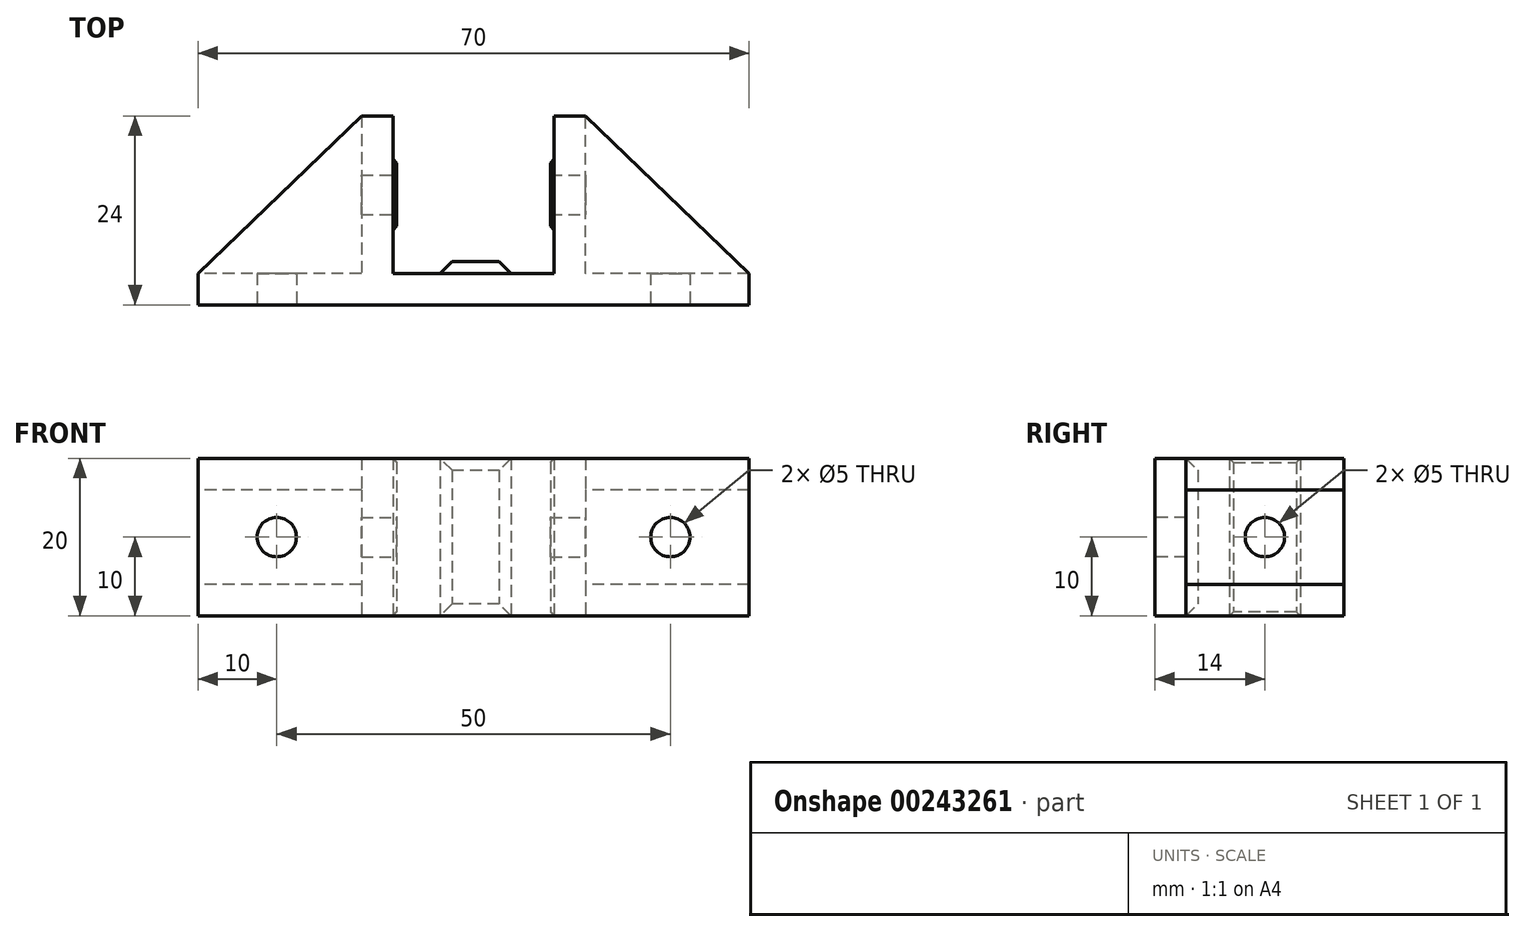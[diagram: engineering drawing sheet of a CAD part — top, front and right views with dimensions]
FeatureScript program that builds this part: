
annotation { "Feature Type Name" : "Feature", "Feature Type Description" : "" }
export const myFeature = defineFeature(function(context is Context, id is Id, definition is map)
    precondition{}
    {
        {
            var Q0;
            Q0=qCreatedBy(makeId("Top.planeOp"),FACE);
            var sketch = newSketch(context, id + "F0", { "sketchPlane" : qUnion([Q0])});
            skLineSegment(sketch, "E0", {"start": v(0, 0) * mm, "end": v(70, 0) * mm});
            skLineSegment(sketch, "E1", {"start": v(70, 0) * mm, "end": v(70, 4) * mm});
            skLineSegment(sketch, "E2", {"start": v(70, 4) * mm, "end": v(49.25, 4) * mm});
            skLineSegment(sketch, "E3", {"start": v(49.25, 4) * mm, "end": v(49.25, 24) * mm});
            skLineSegment(sketch, "E4", {"start": v(49.25, 24) * mm, "end": v(45.25, 24) * mm});
            skLineSegment(sketch, "E5", {"start": v(45.25, 24) * mm, "end": v(45.25, 18.5) * mm});
            skLineSegment(sketch, "E6", {"start": v(45.25, 4) * mm, "end": v(39.75, 4) * mm});
            skLineSegment(sketch, "E7", {"start": v(24.75, 4) * mm, "end": v(24.75, 9.5) * mm});
            skLineSegment(sketch, "E8", {"start": v(24.75, 24) * mm, "end": v(20.75, 24) * mm});
            skLineSegment(sketch, "E9", {"start": v(20.75, 24) * mm, "end": v(20.75, 4) * mm});
            skLineSegment(sketch, "E10", {"start": v(20.75, 4) * mm, "end": v(0, 4) * mm});
            skLineSegment(sketch, "E11", {"start": v(0, 4) * mm, "end": v(0, 0) * mm});
            skLineSegment(sketch, "E12", {"start": v(24.75, 18.5) * mm, "end": v(25.25, 18) * mm});
            skLineSegment(sketch, "E13", {"start": v(25.25, 18) * mm, "end": v(25.25, 10) * mm});
            skLineSegment(sketch, "E14", {"start": v(25.25, 10) * mm, "end": v(24.75, 9.5) * mm});
            skLineSegment(sketch, "E15", {"start": v(35, 4) * mm, "end": v(35, 25.01) * mm, "construction": true});
            skLineSegment(sketch, "E16.MirrorCS", {"start": v(44.75, 10) * mm, "end": v(45.25, 9.5) * mm});
            skLineSegment(sketch, "E17.MirrorCS", {"start": v(45.25, 18.5) * mm, "end": v(44.75, 18) * mm});
            skLineSegment(sketch, "E18.MirrorCS", {"start": v(44.75, 18) * mm, "end": v(44.75, 10) * mm});
            skLineSegment(sketch, "E19.trimOffspring", {"start": v(24.75, 18.5) * mm, "end": v(24.75, 24) * mm});
            skLineSegment(sketch, "E20.trimOffspring", {"start": v(45.25, 9.5) * mm, "end": v(45.25, 4) * mm});
            skLineSegment(sketch, "E21", {"start": v(30.75, 4) * mm, "end": v(32.25, 5.5) * mm});
            skLineSegment(sketch, "E22", {"start": v(32.25, 5.5) * mm, "end": v(38.25, 5.5) * mm});
            skLineSegment(sketch, "E23", {"start": v(38.25, 5.5) * mm, "end": v(39.75, 4) * mm});
            skLineSegment(sketch, "E24.trimOffspring", {"start": v(30.75, 4) * mm, "end": v(24.75, 4) * mm});
            skSolve(sketch);
        }
        {
            var Q0;
            Q0 = qSketchRegion(id + "F0", true);
            extrude(context, id + "F1", {"entities" : qUnion([Q0]), "depth" : 20 * mm});
        }
        {
            var Q0;
            Q0=makeQuery(id+"F1.opExtrude","SWEPT_FACE",FACE,{"disambiguationData":[OSD([sQuery(id+"F0.wireOp",EDGE,"E0")])]});
            var sketch = newSketch(context, id + "F2", { "sketchPlane" : qUnion([Q0])});
            skCircle(sketch, "E25", {"center": v(10, 10) * mm, "radius": 2.5 * mm});
            skPoint(sketch, "E25.centerSnap0", {"position": v(0, 10) * mm});
            skCircle(sketch, "E26", {"center": v(60, 10) * mm, "radius": 2.5 * mm});
            skSolve(sketch);
        }
        {
            var Q0;
            Q0 = qSketchRegion(id + "F2", true);
            extrude(context, id + "F3", {"entities" : qUnion([Q0]), "operationType" : NewBodyOperationType.REMOVE, "endBound" : BoundingType.THROUGH_ALL, "oppositeDirection" : true, "depth" : 25 * mm});
        }
        {
            var Q0;
            Q0=makeQuery(id+"F1.opExtrude","CAP_EDGE",EDGE,{"disambiguationData":[OSD([sQuery(id+"F0.wireOp",EDGE,"E13")])],"isStart":false});
            var Q1;
            Q1=makeQuery(id+"F1.opExtrude","CAP_EDGE",EDGE,{"disambiguationData":[OSD([sQuery(id+"F0.wireOp",EDGE,"E13")])],"isStart":true});
            var Q2;
            Q2=makeQuery(id+"F1.opExtrude","CAP_EDGE",EDGE,{"disambiguationData":[OSD([sQuery(id+"F0.wireOp",EDGE,"E18.MirrorCS")])],"isStart":false});
            var Q3;
            Q3=makeQuery(id+"F1.opExtrude","CAP_EDGE",EDGE,{"disambiguationData":[OSD([sQuery(id+"F0.wireOp",EDGE,"E18.MirrorCS")])],"isStart":true});
            chamfer(context, id + "F4", {"entities" : qUnion([Q0, Q1, Q2, Q3]), "width" : 0.5 * mm, "tangentPropagation" : true});
        }
        {
            var Q0;
            Q0=makeQuery(id+"F1.opExtrude","SWEPT_FACE",FACE,{"disambiguationData":[OSD([sQuery(id+"F0.wireOp",EDGE,"E3")])]});
            var sketch = newSketch(context, id + "F5", { "sketchPlane" : qUnion([Q0])});
            skLineSegment(sketch, "E27.0.0", {"start": v(18, 19.5) * mm, "end": v(18, 0.5) * mm, "construction": true});
            skLineSegment(sketch, "E27.0.1", {"start": v(18, 0.5) * mm, "end": v(10, 0.5) * mm, "construction": true});
            skLineSegment(sketch, "E27.0.2", {"start": v(10, 0.5) * mm, "end": v(10, 19.5) * mm, "construction": true});
            skLineSegment(sketch, "E27.0.3", {"start": v(10, 19.5) * mm, "end": v(18, 19.5) * mm, "construction": true});
            skCircle(sketch, "E28", {"center": v(14, 10) * mm, "radius": 2.5 * mm});
            skPoint(sketch, "E28.centerSnap0", {"position": v(10, 10) * mm});
            skPoint(sketch, "E28.centerSnap1", {"position": v(14, 19.5) * mm});
            skSolve(sketch);
        }
        {
            var Q0;
            Q0 = qSketchRegion(id + "F5", true);
            var Q1;
            Q1=makeQuery(id+"F1.opExtrude","SWEPT_FACE",FACE,{"disambiguationData":[OSD([sQuery(id+"F0.wireOp",EDGE,"E9")])]});
            extrude(context, id + "F6", {"entities" : qUnion([Q0]), "operationType" : NewBodyOperationType.REMOVE, "endBound" : BoundingType.UP_TO_SURFACE, "oppositeDirection" : true, "endBoundEntityFace" : qUnion([Q1]), "depth" : 25 * mm});
        }
        {
            var Q0;
            Q0=makeQuery(id+"F1.opExtrude","CAP_FACE",FACE,{"disambiguationData":[OSD([sQuery(id+"F0.wireOp",EDGE,"E0"),sQuery(id+"F0.wireOp",EDGE,"E1"),sQuery(id+"F0.wireOp",EDGE,"E2"),sQuery(id+"F0.wireOp",EDGE,"E3"),sQuery(id+"F0.wireOp",EDGE,"E4"),sQuery(id+"F0.wireOp",EDGE,"E5"),sQuery(id+"F0.wireOp",EDGE,"E6"),sQuery(id+"F0.wireOp",EDGE,"E7"),sQuery(id+"F0.wireOp",EDGE,"E8"),sQuery(id+"F0.wireOp",EDGE,"E9"),sQuery(id+"F0.wireOp",EDGE,"E10"),sQuery(id+"F0.wireOp",EDGE,"E11"),sQuery(id+"F0.wireOp",EDGE,"E12"),sQuery(id+"F0.wireOp",EDGE,"E13"),sQuery(id+"F0.wireOp",EDGE,"E14"),sQuery(id+"F0.wireOp",EDGE,"E16.MirrorCS"),sQuery(id+"F0.wireOp",EDGE,"E17.MirrorCS"),sQuery(id+"F0.wireOp",EDGE,"E18.MirrorCS"),sQuery(id+"F0.wireOp",EDGE,"E19.trimOffspring"),sQuery(id+"F0.wireOp",EDGE,"E20.trimOffspring"),sQuery(id+"F0.wireOp",EDGE,"E21"),sQuery(id+"F0.wireOp",EDGE,"E22"),sQuery(id+"F0.wireOp",EDGE,"E23"),sQuery(id+"F0.wireOp",EDGE,"E24.trimOffspring")])],"isStart":false});
            var sketch = newSketch(context, id + "F7", { "sketchPlane" : qUnion([Q0])});
            skLineSegment(sketch, "E29", {"start": v(20.75, 24) * mm, "end": v(0, 4) * mm});
            skLineSegment(sketch, "E30", {"start": v(0, 4) * mm, "end": v(20.75, 4) * mm});
            skLineSegment(sketch, "E31", {"start": v(20.75, 4) * mm, "end": v(20.75, 24) * mm});
            skLineSegment(sketch, "E32", {"start": v(49.25, 24) * mm, "end": v(49.25, 4) * mm});
            skLineSegment(sketch, "E33", {"start": v(49.25, 4) * mm, "end": v(70, 4) * mm});
            skLineSegment(sketch, "E34", {"start": v(70, 4) * mm, "end": v(49.25, 24) * mm});
            skSolve(sketch);
        }
        {
            var Q0;
            Q0 = qSketchRegion(id + "F7", true);
            extrude(context, id + "F8", {"entities" : qUnion([Q0]), "operationType" : NewBodyOperationType.ADD, "oppositeDirection" : true, "depth" : 4 * mm});
        }
        {
            var Q0;
            Q0=makeQuery(id+"F1.opExtrude","CAP_FACE",FACE,{"disambiguationData":[OSD([sQuery(id+"F0.wireOp",EDGE,"E0"),sQuery(id+"F0.wireOp",EDGE,"E1"),sQuery(id+"F0.wireOp",EDGE,"E2"),sQuery(id+"F0.wireOp",EDGE,"E3"),sQuery(id+"F0.wireOp",EDGE,"E4"),sQuery(id+"F0.wireOp",EDGE,"E5"),sQuery(id+"F0.wireOp",EDGE,"E6"),sQuery(id+"F0.wireOp",EDGE,"E7"),sQuery(id+"F0.wireOp",EDGE,"E8"),sQuery(id+"F0.wireOp",EDGE,"E9"),sQuery(id+"F0.wireOp",EDGE,"E10"),sQuery(id+"F0.wireOp",EDGE,"E11"),sQuery(id+"F0.wireOp",EDGE,"E12"),sQuery(id+"F0.wireOp",EDGE,"E13"),sQuery(id+"F0.wireOp",EDGE,"E14"),sQuery(id+"F0.wireOp",EDGE,"E16.MirrorCS"),sQuery(id+"F0.wireOp",EDGE,"E17.MirrorCS"),sQuery(id+"F0.wireOp",EDGE,"E18.MirrorCS"),sQuery(id+"F0.wireOp",EDGE,"E19.trimOffspring"),sQuery(id+"F0.wireOp",EDGE,"E20.trimOffspring"),sQuery(id+"F0.wireOp",EDGE,"E21"),sQuery(id+"F0.wireOp",EDGE,"E22"),sQuery(id+"F0.wireOp",EDGE,"E23"),sQuery(id+"F0.wireOp",EDGE,"E24.trimOffspring")])],"isStart":true});
            var sketch = newSketch(context, id + "F9", { "sketchPlane" : qUnion([Q0])});
            skLineSegment(sketch, "E35.0.0", {"start": v(20.75, -24) * mm, "end": v(20.75, -4) * mm});
            skLineSegment(sketch, "E35.0.1", {"start": v(20.75, -4) * mm, "end": v(0, -4) * mm});
            skLineSegment(sketch, "E35.0.2", {"start": v(0, -4) * mm, "end": v(20.75, -24) * mm});
            skLineSegment(sketch, "E36.0.0", {"start": v(70, -4) * mm, "end": v(49.25, -4) * mm});
            skLineSegment(sketch, "E36.0.1", {"start": v(49.25, -4) * mm, "end": v(49.25, -24) * mm});
            skLineSegment(sketch, "E36.0.2", {"start": v(49.25, -24) * mm, "end": v(70, -4) * mm});
            skSolve(sketch);
        }
        {
            var Q0;
            Q0 = qSketchRegion(id + "F9", true);
            extrude(context, id + "F10", {"entities" : qUnion([Q0]), "operationType" : NewBodyOperationType.ADD, "oppositeDirection" : true, "depth" : 4 * mm});
        }
        {
            var Q0;
            Q0=makeQuery(id+"F1.opExtrude","CAP_EDGE",EDGE,{"disambiguationData":[OSD([sQuery(id+"F0.wireOp",EDGE,"E22")])],"isStart":false});
            var Q1;
            Q1=makeQuery(id+"F1.opExtrude","CAP_EDGE",EDGE,{"disambiguationData":[OSD([sQuery(id+"F0.wireOp",EDGE,"E22")])],"isStart":true});
            chamfer(context, id + "F11", {"entities" : qUnion([Q0, Q1]), "width" : 1.5 * mm, "tangentPropagation" : true});
        }
    });
